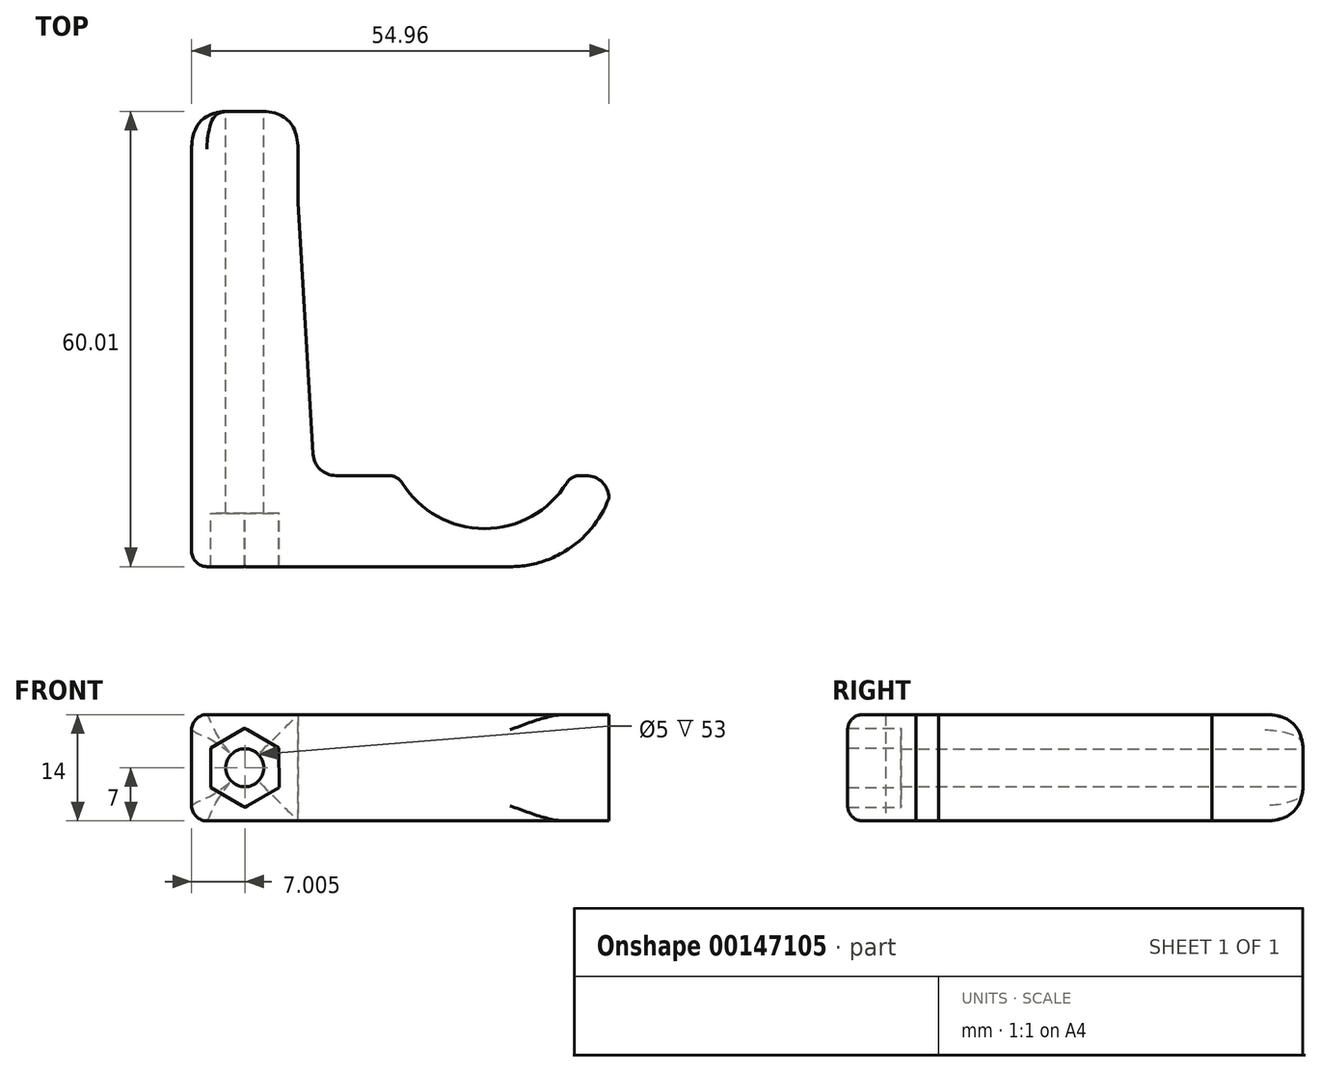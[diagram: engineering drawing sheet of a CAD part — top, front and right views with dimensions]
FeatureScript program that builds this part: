
annotation { "Feature Type Name" : "Feature", "Feature Type Description" : "" }
export const myFeature = defineFeature(function(context is Context, id is Id, definition is map)
    precondition{}
    {
        {
            var Q0;
            Q0=qCreatedBy(makeId("Top.planeOp"),FACE);
            var sketch = newSketch(context, id + "F0", { "sketchPlane" : qUnion([Q0])});
            skCircle(sketch, "E0", {"center": v(0, 0) * mm, "radius": 12.56 * mm, "construction": true});
            skLineSegment(sketch, "E1", {"start": v(-24.57, 30.23) * mm, "end": v(-24.57, 42.23) * mm});
            skLineSegment(sketch, "E2", {"start": v(-24.57, 42.23) * mm, "end": v(-38.57, 42.23) * mm});
            skLineSegment(sketch, "E3", {"start": v(-38.57, 42.23) * mm, "end": v(-38.56, -17.77) * mm});
            skLineSegment(sketch, "E4", {"start": v(-38.56, -17.77) * mm, "end": v(16.39, -17.77) * mm});
            skLineSegment(sketch, "E5", {"start": v(16.39, -17.77) * mm, "end": v(16.39, -5.76) * mm});
            skArc(sketch, "E6.0", {"start": v(-11.39, -5.77) * mm, "mid": v(0, -12.77) * mm, "end": v(11.39, -5.77) * mm});
            skLineSegment(sketch, "E7", {"start": v(16.39, -5.76) * mm, "end": v(11.39, -5.76) * mm});
            skLineSegment(sketch, "E8", {"start": v(-11.39, -5.76) * mm, "end": v(-22.39, -5.76) * mm});
            skLineSegment(sketch, "E9", {"start": v(-22.39, -5.77) * mm, "end": v(-24.56, 30.23) * mm});
            skLineSegment(sketch, "E10", {"start": v(-31.57, 42.23) * mm, "end": v(-31.56, -17.77) * mm, "construction": true});
            skSolve(sketch);
        }
        {
            var Q0;
            Q0=makeQuery(id+"F0.imprint","IMPRINT",FACE,{"disambiguationData":[TD([[makeQuery(id+"F0.imprint","IMPRINT",EDGE,{"derivedFrom":sQuery(id+"F0.wireOp",EDGE,"E1")}),1.0]])]});
            extrude(context, id + "F1", {"entities" : qUnion([Q0]), "depth" : 14 * mm});
        }
        {
            var Q0;
            Q0=makeQuery(id+"F1.opExtrude","SWEPT_FACE",FACE,{"disambiguationData":[OSD([sQuery(id+"F0.wireOp",EDGE,"E2")])]});
            var sketch = newSketch(context, id + "F2", { "sketchPlane" : qUnion([Q0])});
            skLineSegment(sketch, "E11", {"start": v(24.56, 14) * mm, "end": v(38.56, 0) * mm, "construction": true});
            skLineSegment(sketch, "E12", {"start": v(31.56, 14) * mm, "end": v(31.56, 0) * mm, "construction": true});
            skCircle(sketch, "E13", {"center": v(31.56, 7) * mm, "radius": 2.5 * mm});
            skCircle(sketch, "E14.cCircle", {"center": v(31.56, 7) * mm, "radius": 4.5 * mm, "construction": true});
            skLineSegment(sketch, "E14.0", {"start": v(36.06, 4.39) * mm, "end": v(31.55, 1.8) * mm});
            skLineSegment(sketch, "E14.1", {"start": v(31.55, 1.8) * mm, "end": v(27.06, 4.42) * mm});
            skLineSegment(sketch, "E14.2", {"start": v(27.06, 4.42) * mm, "end": v(27.07, 9.61) * mm});
            skLineSegment(sketch, "E14.3", {"start": v(27.07, 9.61) * mm, "end": v(31.58, 12.2) * mm});
            skLineSegment(sketch, "E14.4", {"start": v(31.58, 12.2) * mm, "end": v(36.07, 9.58) * mm});
            skLineSegment(sketch, "E14.5", {"start": v(36.07, 9.58) * mm, "end": v(36.06, 4.39) * mm});
            skPoint(sketch, "E14.0.midPoint", {"position": v(33.8, 3.1) * mm});
            skSolve(sketch);
        }
        {
            var Q0;
            Q0=makeQuery(id+"F2.imprint","IMPRINT",FACE,{"disambiguationData":[TD([[makeQuery(id+"F2.imprint","IMPRINT",EDGE,{"derivedFrom":sQuery(id+"F2.wireOp",EDGE,"E13")}),1.0]])]});
            var Q1;
            Q1=sQuery(id+"F2.wireOp",EDGE,"E13");
            extrude(context, id + "F3", {"entities" : qUnion([Q0]), "operationType" : NewBodyOperationType.REMOVE, "surfaceEntities" : qUnion([Q1]), "endBound" : BoundingType.UP_TO_NEXT, "oppositeDirection" : true, "depth" : 31 * mm});
        }
        {
            var Q0;
            Q0=makeQuery(id+"F1.opExtrude","SWEPT_EDGE",EDGE,{"disambiguationData":[OSD([sQuery(id+"F0.wireOp",EDGE,"E5"),sQuery(id+"F0.wireOp",EDGE,"E7")])]});
            var Q1;
            Q1=makeQuery(id+"F1.opExtrude","SWEPT_EDGE",EDGE,{"disambiguationData":[OSD([sQuery(id+"F0.wireOp",EDGE,"E8"),sQuery(id+"F0.wireOp",EDGE,"E9")])]});
            fillet(context, id + "F4", {"entities" : qUnion([Q0, Q1]), "radius" : 3 * mm, "allowEdgeOverflow" : false});
        }
        {
            var Q0;
            Q0=makeQuery(id+"F1.opExtrude","SWEPT_EDGE",EDGE,{"disambiguationData":[OSD([sQuery(id+"F0.wireOp",EDGE,"E6.0"),sQuery(id+"F0.wireOp",EDGE,"E8")])]});
            var Q1;
            Q1=makeQuery(id+"F1.opExtrude","SWEPT_EDGE",EDGE,{"disambiguationData":[OSD([sQuery(id+"F0.wireOp",EDGE,"E6.0"),sQuery(id+"F0.wireOp",EDGE,"E7")])]});
            var Q2;
            Q2=makeQuery(id+"F1.opExtrude","CAP_EDGE",EDGE,{"disambiguationData":[OSD([sQuery(id+"F0.wireOp",EDGE,"E3")])],"isStart":false});
            var Q3;
            Q3=makeQuery(id+"F1.opExtrude","CAP_EDGE",EDGE,{"disambiguationData":[OSD([sQuery(id+"F0.wireOp",EDGE,"E3")])],"isStart":true});
            var Q4;
            Q4=makeQuery(id+"F1.opExtrude","CAP_EDGE",EDGE,{"disambiguationData":[OSD([sQuery(id+"F0.wireOp",EDGE,"E4")])],"isStart":false});
            var Q5;
            Q5=makeQuery(id+"F1.opExtrude","CAP_EDGE",EDGE,{"disambiguationData":[OSD([sQuery(id+"F0.wireOp",EDGE,"E4")])],"isStart":true});
            var Q6;
            Q6=makeQuery(id+"F1.opExtrude","SWEPT_EDGE",EDGE,{"disambiguationData":[OSD([sQuery(id+"F0.wireOp",EDGE,"E3"),sQuery(id+"F0.wireOp",EDGE,"E4")])]});
            var Q7;
            {var subQ0=sQuery(id+"F0.wireOp",EDGE,"E9");Q7=makeQuery(id+"F4.opFillet","BLEND_EDGE",EDGE,{"blendedFrom":[makeQuery(id+"F1.opExtrude","SWEPT_EDGE",EDGE,{"disambiguationData":[OSD([sQuery(id+"F0.wireOp",EDGE,"E1"),subQ0])]}),makeQuery(id+"F1.opExtrude","SWEPT_FACE",FACE,{"disambiguationData":[OSD([subQ0])]})],"blendedInto":[makeQuery(id+"F1.opExtrude","SWEPT_FACE",FACE,{"disambiguationData":[OSD([subQ0])]})]});}
            var Q8;
            {var subQ0=sQuery(id+"F0.wireOp",EDGE,"E1");Q8=makeQuery(id+"F4.opFillet","BLEND_EDGE",EDGE,{"blendedFrom":[makeQuery(id+"F1.opExtrude","SWEPT_EDGE",EDGE,{"disambiguationData":[OSD([subQ0,sQuery(id+"F0.wireOp",EDGE,"E9")])]}),makeQuery(id+"F1.opExtrude","SWEPT_FACE",FACE,{"disambiguationData":[OSD([subQ0])]})],"blendedInto":[makeQuery(id+"F1.opExtrude","SWEPT_FACE",FACE,{"disambiguationData":[OSD([subQ0])]})]});}
            fillet(context, id + "F5", {"entities" : qUnion([Q0, Q1, Q2, Q3, Q4, Q5, Q6, Q7, Q8]), "radius" : 2 * mm, "allowEdgeOverflow" : false});
        }
        {
            var Q0;
            Q0=makeQuery(id+"F1.opExtrude","SWEPT_EDGE",EDGE,{"disambiguationData":[OSD([sQuery(id+"F0.wireOp",EDGE,"E4"),sQuery(id+"F0.wireOp",EDGE,"E5")])]});
            fillet(context, id + "F6", {"entities" : qUnion([Q0]), "radius" : 13.88 * mm, "allowEdgeOverflow" : false});
        }
        {
            var Q0;
            Q0 = qSketchRegion(id + "F2", true);
            extrude(context, id + "F7", {"entities" : qUnion([Q0]), "operationType" : NewBodyOperationType.REMOVE, "oppositeDirection" : true, "depth" : 60 * mm, "hasSecondDirection" : true, "secondDirectionOppositeDirection" : true, "secondDirectionDepth" : 53 * mm});
        }
        {
            var Q0;
            Q0=makeQuery(id+"F1.opExtrude","CAP_EDGE",EDGE,{"disambiguationData":[OSD([sQuery(id+"F0.wireOp",EDGE,"E2")])],"isStart":false});
            var Q1;
            Q1=makeQuery(id+"F1.opExtrude","SWEPT_EDGE",EDGE,{"disambiguationData":[OSD([sQuery(id+"F0.wireOp",EDGE,"E1"),sQuery(id+"F0.wireOp",EDGE,"E2")])]});
            var Q2;
            Q2=makeQuery(id+"F1.opExtrude","CAP_EDGE",EDGE,{"disambiguationData":[OSD([sQuery(id+"F0.wireOp",EDGE,"E2")])],"isStart":true});
            var Q3;
            Q3=makeQuery(id+"F1.opExtrude","SWEPT_EDGE",EDGE,{"disambiguationData":[OSD([sQuery(id+"F0.wireOp",EDGE,"E2"),sQuery(id+"F0.wireOp",EDGE,"E3")])]});
            fillet(context, id + "F8", {"entities" : qUnion([Q0, Q1, Q2, Q3]), "radius" : 5 * mm, "tangentPropagation" : true, "rho" : .5, "crossSection" : FilletCrossSection.CONIC, "allowEdgeOverflow" : false});
        }
    });
